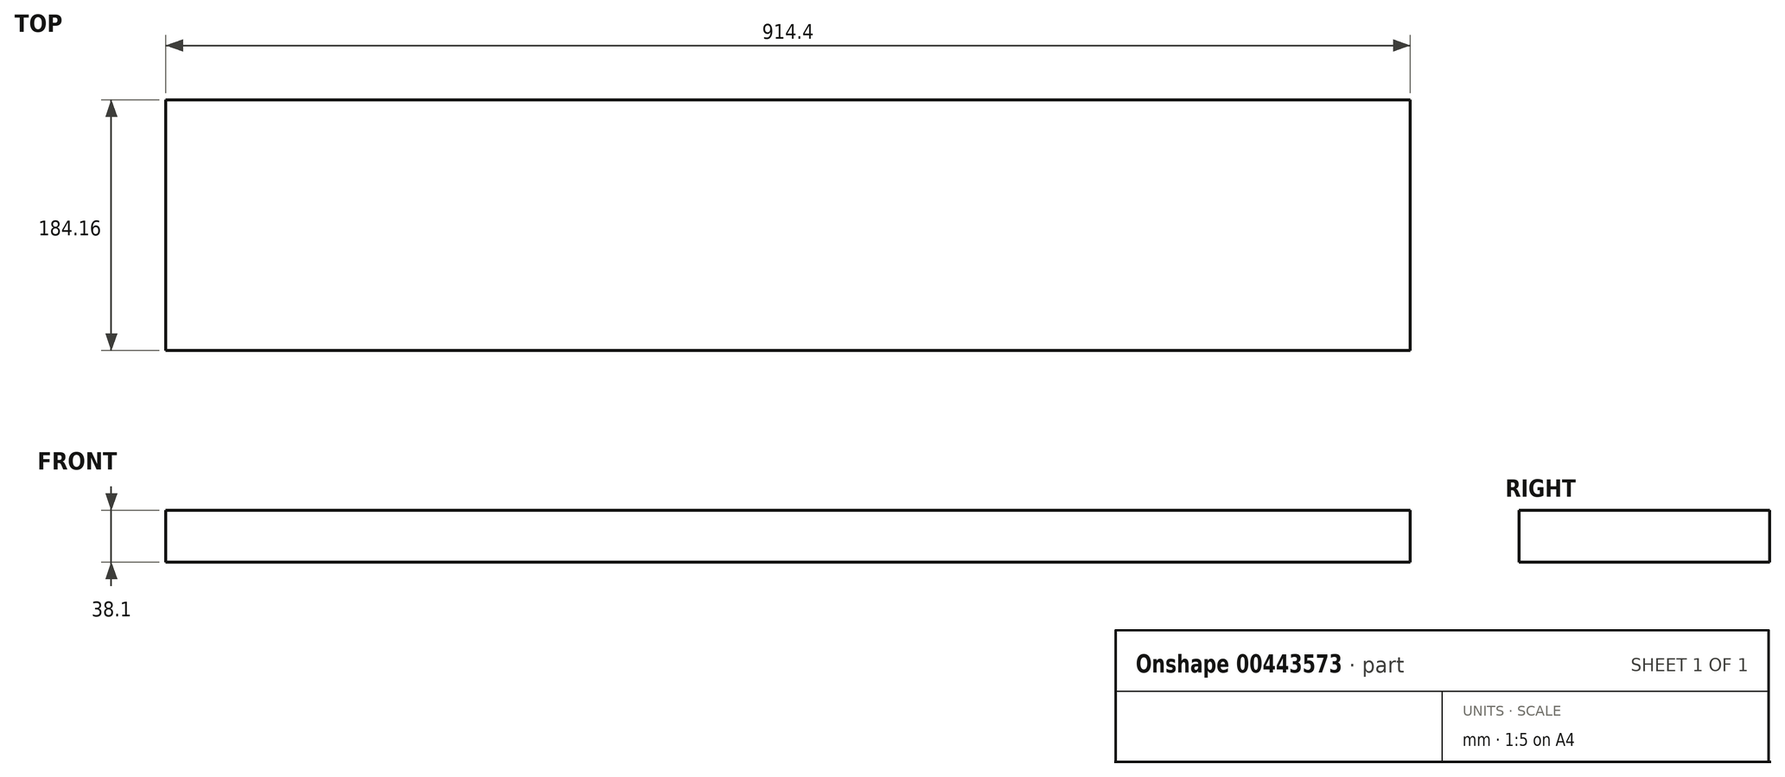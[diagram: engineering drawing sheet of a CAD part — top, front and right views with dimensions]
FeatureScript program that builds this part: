
annotation { "Feature Type Name" : "Feature", "Feature Type Description" : "" }
export const myFeature = defineFeature(function(context is Context, id is Id, definition is map)
    precondition{}
    {
        {
            var Q0;
            Q0=qCreatedBy(makeId("Top.planeOp"),FACE);
            var sketch = newSketch(context, id + "F0", { "sketchPlane" : qUnion([Q0])});
            skLineSegment(sketch, "E0.bottom", {"start": v(-457.2, 92.08) * mm, "end": v(457.2, 92.08) * mm});
            skLineSegment(sketch, "E0.top", {"start": v(-457.2, -92.08) * mm, "end": v(457.2, -92.08) * mm});
            skLineSegment(sketch, "E0.left", {"start": v(-457.2, 92.08) * mm, "end": v(-457.2, -92.08) * mm});
            skLineSegment(sketch, "E0.right", {"start": v(457.2, 92.08) * mm, "end": v(457.2, -92.08) * mm});
            skSolve(sketch);
        }
        {
            var Q0;
            Q0=makeQuery(id+"F0.imprint","IMPRINT",FACE,{"disambiguationData":[TD([[makeQuery(id+"F0.imprint","IMPRINT",EDGE,{"derivedFrom":sQuery(id+"F0.wireOp",EDGE,"E0.bottom")}),-1.0]])]});
            extrude(context, id + "F1", {"entities" : qUnion([Q0]), "depth" : (1.5 * 25.4) * mm});
        }
    });
